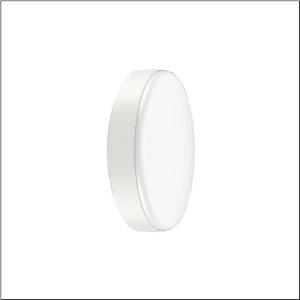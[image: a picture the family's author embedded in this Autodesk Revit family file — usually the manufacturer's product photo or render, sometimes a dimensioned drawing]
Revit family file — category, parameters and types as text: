
# Revit family: rondel_31_51wc10db34a
name_source: partatom
category: Lighting Fixtures
units: mm (PartAtom-declared; Revit-internal decimal feet)

## family parameters
Cut with Voids When Loaded = No
Host = Face
Light Source = No
Part Type = Normal
Room Calculation Point = No
Round Connector Dimension = Use Diameter
Shared = No

## types (1)
- Rondel 31 (1 x LED, 4250 lm, 34 W, 3000K)
    Apparent Load = 34 VA
    CIE Flux Codes = 44 75 94 94 100
    Color Rendering = 80
    Color Temperature = 3000K
    Default Elevation = 1800 mm
    Description = Rondel 31, wall and ceiling luminaire, primary optical cover: cover, of PC, opal, light emission: direct distribution, primary light characteristic: symmetric, installation type: surface-mounted, LED, rated luminous flux: 4.250lm, luminous efficacy: 125lm/W, light colour: 830, colour temperature: 3000K, with terminal, 5-pole, max. 2.5mm², mains connection: 220..240V, AC, 50/60Hz, rated input power: 34W, luminaire housing, of PC, traffic white (RAL 9016), diameter: 480mm, protection rating (complete): IP65, insulation class (complete): insulation class II (safety insulation), certification: CE, impact resistance: IK10, permissible operating ambient temperature: -20..+40°C, permissible storage temperature: -20..+60°C, packaging unit: 1 piece
    Height = 97 mm
    Lamp = 1 x LED
    Lamp Light Flux = 4250 lm
    Lamp Power = 34 W
    Lamp count = 1
    Length = 480 mm
    Luminous efficacy = 125 lm/W
    Manufacturer = Siteco
    ModVariant = No
    Model = 51WC10DB34A
    Mounting Place = Ceiling
    Mounting Type = Surface mounted
    Number of Poles = 1
    OnlyDefault = Yes
    Power Factor = 1
    Product Name = Rondel 31
    Product group = wall and ceiling luminaire
    ProductGroupID = 301
    Protection Class = Protection class II
    Protection Degree = IP 65
    RLX_Detail_Level = 1
    RLX_Emergency_Light_Flux = 0 lm
    RLX_Emergency_Type = 0
    RLX_Emergency_Type_DB = No
    RlxData = <blob elided: 40777 chars, md5=4a629ab8>
    Socket = socket
    Standby Power = 0 W
    System Light Flux = 4250 lm
    System Power = 34 W
    Type Comments = Product without accessories
    Type Image = l_1007188.jpg
    URL = http://relux.com
    VarID = ---
    Voltage = 0 V
    Weight = 0.00 kg
    Width = 0 mm  [stored 0 ft]

note: [stored X ft] marks values corroborated as IEEE doubles in the binary element streams (Revit-internal decimal feet)

## geometry (parser evidence)
native form markers: Blend x4, Sweep x14
no freeform markers — native parametric forms only
